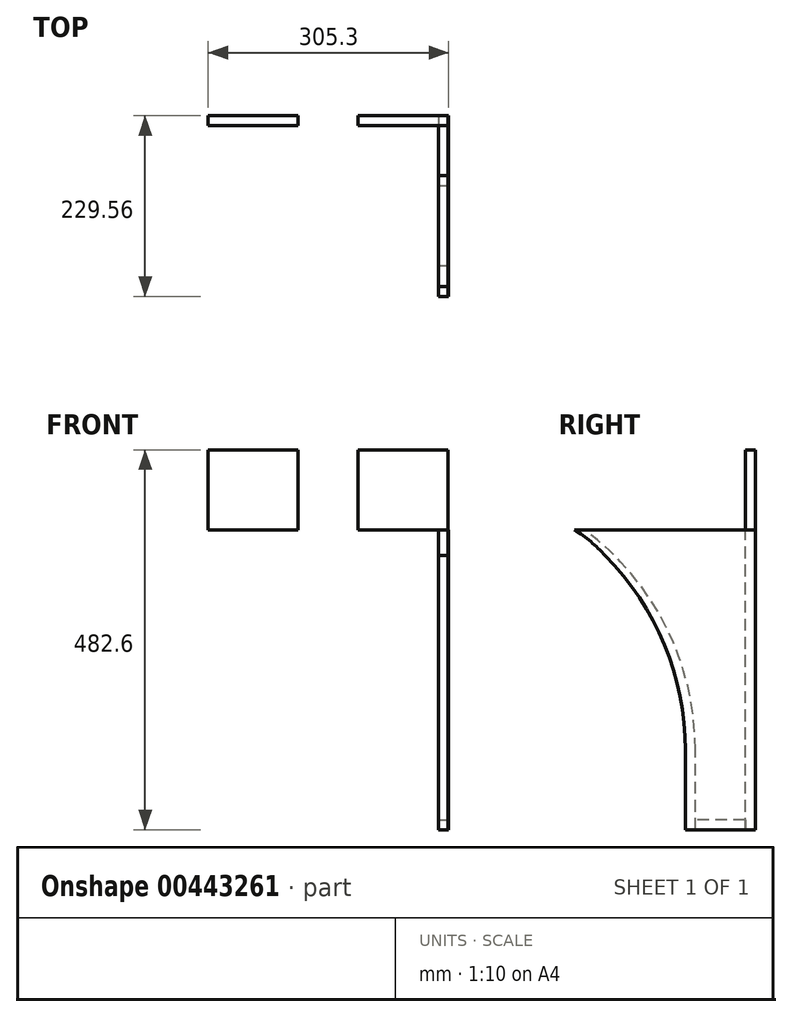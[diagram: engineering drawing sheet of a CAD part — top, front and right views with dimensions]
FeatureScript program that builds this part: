
annotation { "Feature Type Name" : "Feature", "Feature Type Description" : "" }
export const myFeature = defineFeature(function(context is Context, id is Id, definition is map)
    precondition{}
    {
        {
            var Q0;
            Q0=qCreatedBy(makeId("Right.planeOp"),FACE);
            var sketch = newSketch(context, id + "F0", { "sketchPlane" : qUnion([Q0])});
            skLineSegment(sketch, "E0", {"start": v(0, 0) * mm, "end": v(88.9, 0) * mm});
            skPoint(sketch, "E1", {"position": v(44.45, 0) * mm});
            skLineSegment(sketch, "E2", {"start": v(0, 101.6) * mm, "end": v(0, 0) * mm});
            skLineSegment(sketch, "E3", {"start": v(88.9, 0) * mm, "end": v(88.9, 101.6) * mm});
            skPoint(sketch, "E4.endSnap0", {"position": v(88.9, 50.8) * mm});
            skLineSegment(sketch, "E5", {"start": v(88.9, 381) * mm, "end": v(-140.66, 381) * mm});
            skLineSegment(sketch, "E6", {"start": v(12.7, 101.6) * mm, "end": v(12.7, 0) * mm});
            skLineSegment(sketch, "E7", {"start": v(12.7, 12.7) * mm, "end": v(76.2, 12.7) * mm});
            skLineSegment(sketch, "E8", {"start": v(76.2, 0) * mm, "end": v(76.2, 101.6) * mm});
            skLineSegment(sketch, "E9", {"start": v(88.9, 101.6) * mm, "end": v(88.9, 381) * mm});
            skArc(sketch, "E10", {"start": v(-63.64, 282.36) * mm, "mid": v(-93.45, 338.47) * mm, "end": v(-140.66, 381) * mm});
            skArc(sketch, "E11", {"start": v(0, 101.6) * mm, "mid": v(-26.43, 235.05) * mm, "end": v(-101.74, 348.35) * mm});
            skLineSegment(sketch, "E12", {"start": v(76.2, 101.6) * mm, "end": v(76.2, 368.3) * mm});
            skLineSegment(sketch, "E13", {"start": v(76.2, 368.3) * mm, "end": v(76.2, 381) * mm});
            skPoint(sketch, "E14", {"position": v(-127.96, 381) * mm});
            skArc(sketch, "E15", {"start": v(12.7, 101.6) * mm, "mid": v(-24.45, 258) * mm, "end": v(-127.96, 381) * mm});
            skLineSegment(sketch, "E16", {"start": v(88.9, 381) * mm, "end": v(88.9, 482.6) * mm});
            skLineSegment(sketch, "E17", {"start": v(88.9, 482.6) * mm, "end": v(76.2, 482.6) * mm});
            skLineSegment(sketch, "E18", {"start": v(76.2, 482.6) * mm, "end": v(76.2, 381) * mm});
            skSolve(sketch);
        }
        {
            assignVariable(context, id + "F1", {"name" : "thick", "anyValue" : 0.5});
        }
        {
            var Q0;
            {var subQ6=sQuery(id+"F0.wireOp",EDGE,"E2");Q0=makeQuery(id+"F0.imprint","IMPRINT",FACE,{"disambiguationData":[TD([[makeQuery(id+"F0.imprint","IMPRINT",EDGE,{"derivedFrom":subQ6}),1.0]])]});}
            var Q1;
            {var subQ5=sQuery(id+"F0.wireOp",EDGE,"E7");Q1=makeQuery(id+"F0.imprint","IMPRINT",FACE,{"disambiguationData":[TD([[makeQuery(id+"F0.imprint","IMPRINT",EDGE,{"derivedFrom":subQ5}),-1.0]])]});}
            var Q2;
            {var subQ8=sQuery(id+"F0.wireOp",EDGE,"E3");Q2=makeQuery(id+"F0.imprint","IMPRINT",FACE,{"disambiguationData":[TD([[makeQuery(id+"F0.imprint","IMPRINT",EDGE,{"derivedFrom":subQ8}),1.0]])]});}
            var Q3;
            {var subQ1=sQuery(id+"F0.wireOp",EDGE,"E7");Q3=makeQuery(id+"F0.imprint","IMPRINT",FACE,{"disambiguationData":[TD([[makeQuery(id+"F0.imprint","IMPRINT",EDGE,{"derivedFrom":subQ1}),1.0]])]});}
            extrude(context, id + "F2", {"entities" : qUnion([Q0, Q1, Q2, Q3]), "depth" : (getVariable(context, 'thick')) * mm});
        }
        {
            var Q0;
            Q0=makeQuery(id+"F2.opExtrude","SWEPT_BODY",BODY,{"disambiguationData":[OSD([sQuery(id+"F0.wireOp",EDGE,"E0"),sQuery(id+"F0.wireOp",EDGE,"E2"),sQuery(id+"F0.wireOp",EDGE,"E3"),sQuery(id+"F0.wireOp",EDGE,"E5"),sQuery(id+"F0.wireOp",EDGE,"E9"),sQuery(id+"F0.wireOp",EDGE,"E10"),sQuery(id+"F0.wireOp",EDGE,"E11")])]});
            var Q1;
            Q1=makeQuery(id+"F2.opExtrude","SWEPT_EDGE",EDGE,{"disambiguationData":[OSD([sQuery(id+"F0.wireOp",EDGE,"E5"),sQuery(id+"F0.wireOp",EDGE,"E9")])]});
            var Q2;
            Q2=makeQuery(id+"F2.opExtrude","SWEPT_EDGE",EDGE,{"disambiguationData":[OSD([sQuery(id+"F0.wireOp",EDGE,"E5"),sQuery(id+"F0.wireOp",EDGE,"E9")])]});
            transform(context, id + "F3", {"entities" : qUnion([Q0]), "transformType" : TransformType.TRANSLATION_DISTANCE, "transformDirection" : qUnion([Q2]), "distance" : (13 - getVariable(context, 'thick')) * mm, "makeCopy" : true});
        }
        {
            var Q0;
            {var subQ3=sQuery(id+"F0.wireOp",EDGE,"E3");Q0=makeQuery(id+"F0.imprint","IMPRINT",FACE,{"disambiguationData":[TD([[makeQuery(id+"F0.imprint","IMPRINT",EDGE,{"derivedFrom":subQ3}),1.0]])]});}
            extrude(context, id + "F4", {"entities" : qUnion([Q0]), "endBound" : BoundingType.UP_TO_NEXT, "oppositeDirection" : true, "depth" : mm});
        }
        {
            var Q0;
            {var subQ6=sQuery(id+"F0.wireOp",EDGE,"E2");Q0=makeQuery(id+"F0.imprint","IMPRINT",FACE,{"disambiguationData":[TD([[makeQuery(id+"F0.imprint","IMPRINT",EDGE,{"derivedFrom":subQ6}),1.0]])]});}
            extrude(context, id + "F5", {"entities" : qUnion([Q0]), "endBound" : BoundingType.UP_TO_NEXT, "oppositeDirection" : true, "depth" : 25.4 * mm});
        }
        {
            var Q0;
            {var subQ5=sQuery(id+"F0.wireOp",EDGE,"E7");Q0=makeQuery(id+"F0.imprint","IMPRINT",FACE,{"disambiguationData":[TD([[makeQuery(id+"F0.imprint","IMPRINT",EDGE,{"derivedFrom":subQ5}),-1.0]])]});}
            extrude(context, id + "F6", {"entities" : qUnion([Q0]), "endBound" : BoundingType.UP_TO_NEXT, "oppositeDirection" : true, "depth" : 25.4 * mm});
        }
        {
            var Q0;
            {var subQ0=sQuery(id+"F0.wireOp",EDGE,"E16");Q0=makeQuery(id+"F0.imprint","IMPRINT",FACE,{"disambiguationData":[TD([[makeQuery(id+"F0.imprint","IMPRINT",EDGE,{"derivedFrom":subQ0}),1.0]])]});}
            extrude(context, id + "F7", {"entities" : qUnion([Q0]), "operationType" : NewBodyOperationType.ADD, "oppositeDirection" : true, "depth" : 304.8 * mm});
        }
        {
            var Q0;
            Q0=makeQuery(id+"F5.opExtrude","SWEPT_FACE",FACE,{"disambiguationData":[OSD([sQuery(id+"F0.wireOp",EDGE,"E2")])]});
            var sketch = newSketch(context, id + "F8", { "sketchPlane" : qUnion([Q0])});
            skLineSegment(sketch, "E19.bottom", {"start": v(-190.5, 152.4) * mm, "end": v(-114.3, 152.4) * mm});
            skLineSegment(sketch, "E19.top", {"start": v(-190.5, 660.4) * mm, "end": v(-114.3, 660.4) * mm});
            skLineSegment(sketch, "E19.left", {"start": v(-190.5, 152.4) * mm, "end": v(-190.5, 660.4) * mm});
            skLineSegment(sketch, "E19.right", {"start": v(-114.3, 152.4) * mm, "end": v(-114.3, 660.4) * mm});
            skPoint(sketch, "E19.middle", {"position": v(-152.4, 406.4) * mm});
            skPoint(sketch, "E19.middle.positionSnap0", {"position": v(-152.4, 101.6) * mm});
            skPoint(sketch, "E19.centerSnap0", {"position": v(-152.4, 101.6) * mm});
            skSolve(sketch);
        }
        {
            var Q0;
            Q0 = qSketchRegion(id + "F8", true);
            extrude(context, id + "F9", {"entities" : qUnion([Q0]), "operationType" : NewBodyOperationType.REMOVE, "oppositeDirection" : true, "depth" : 508 * mm, "symmetric" : true});
        }
    });
